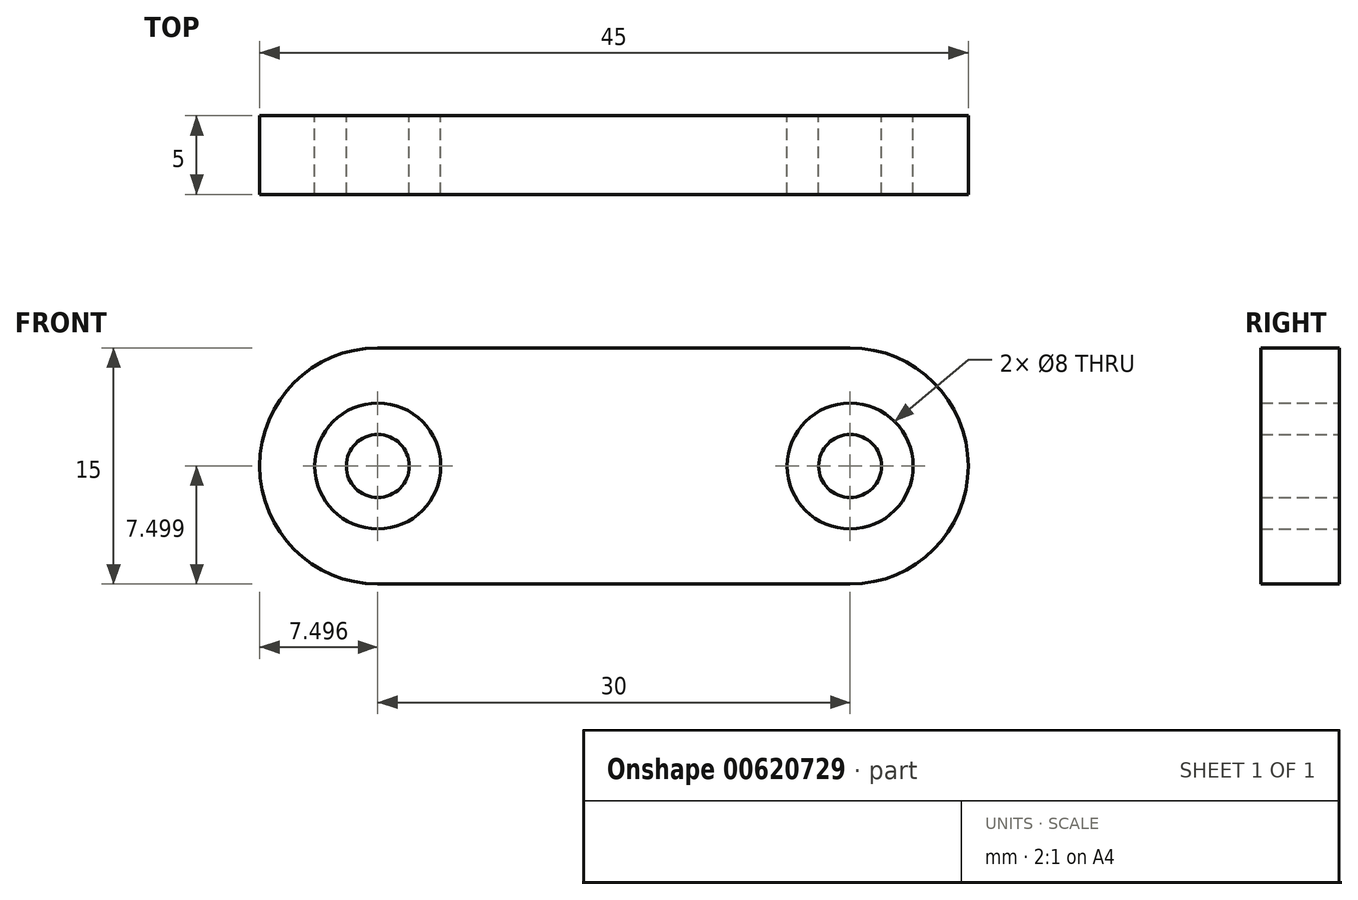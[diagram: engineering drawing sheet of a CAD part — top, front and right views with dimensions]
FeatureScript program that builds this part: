
annotation { "Feature Type Name" : "Feature", "Feature Type Description" : "" }
export const myFeature = defineFeature(function(context is Context, id is Id, definition is map)
    precondition{}
    {
        {
            var Q0;
            Q0=qCreatedBy(makeId("Front.planeOp"),FACE);
            var sketch = newSketch(context, id + "F0", { "sketchPlane" : qUnion([Q0])});
            skLineSegment(sketch, "E0.bottom", {"start": v(-17.01, 14.19) * mm, "end": v(12.99, 14.19) * mm});
            skLineSegment(sketch, "E0.top", {"start": v(-17.01, -0.81) * mm, "end": v(12.99, -0.81) * mm});
            skArc(sketch, "E1", {"start": v(-17.01, 14.19) * mm, "mid": v(-24.51, 6.69) * mm, "end": v(-17.01, -0.81) * mm});
            skArc(sketch, "E2", {"start": v(12.99, -0.81) * mm, "mid": v(20.49, 6.69) * mm, "end": v(12.99, 14.19) * mm});
            skCircle(sketch, "E3", {"center": v(-17.01, 6.69) * mm, "radius": 4 * mm});
            skCircle(sketch, "E4", {"center": v(12.99, 6.69) * mm, "radius": 4 * mm});
            skCircle(sketch, "E5", {"center": v(-17.01, 6.69) * mm, "radius": 2 * mm});
            skCircle(sketch, "E6", {"center": v(12.99, 6.69) * mm, "radius": 2 * mm});
            skSolve(sketch);
        }
        {
            var Q0;
            Q0=makeQuery(id+"F0.imprint","IMPRINT",FACE,{"disambiguationData":[TD([[makeQuery(id+"F0.imprint","IMPRINT",EDGE,{"derivedFrom":sQuery(id+"F0.wireOp",EDGE,"E0.bottom")}),-1.0]])]});
            var Q1;
            Q1=makeQuery(id+"F0.imprint","IMPRINT",FACE,{"disambiguationData":[TD([[makeQuery(id+"F0.imprint","IMPRINT",EDGE,{"derivedFrom":sQuery(id+"F0.wireOp",EDGE,"E5")}),1.0]])]});
            var Q2;
            Q2=makeQuery(id+"F0.imprint","IMPRINT",FACE,{"disambiguationData":[TD([[makeQuery(id+"F0.imprint","IMPRINT",EDGE,{"derivedFrom":sQuery(id+"F0.wireOp",EDGE,"E6")}),1.0]])]});
            extrude(context, id + "F1", {"entities" : qUnion([Q0, Q1, Q2]), "depth" : 5 * mm, "offsetDistance" : 25 * mm});
        }
    });
